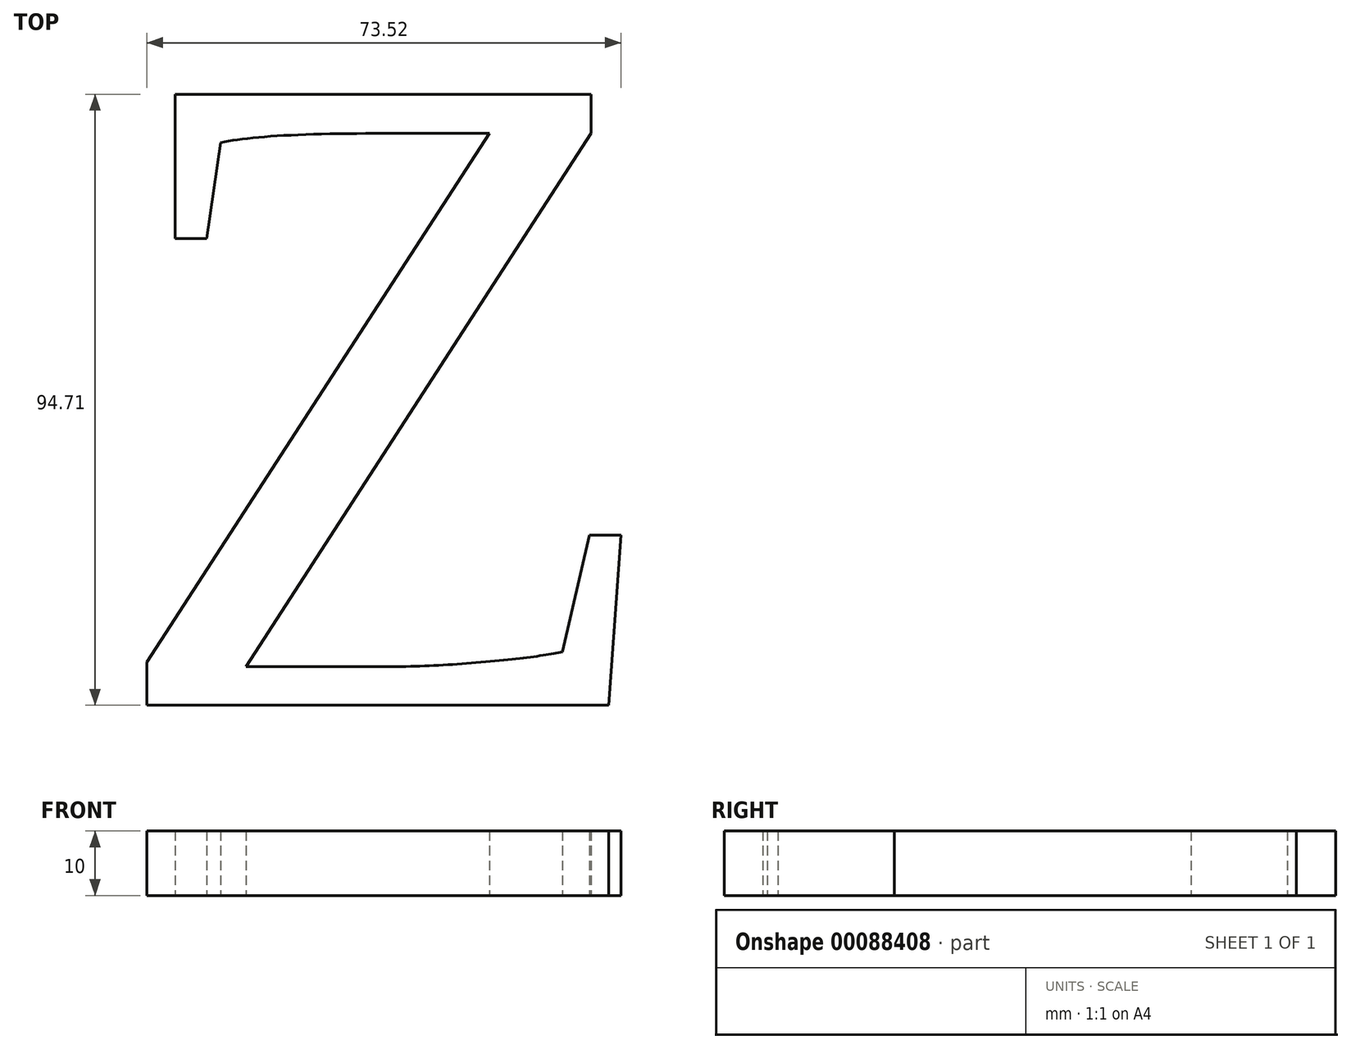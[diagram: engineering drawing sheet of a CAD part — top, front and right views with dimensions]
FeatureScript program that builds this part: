
annotation { "Feature Type Name" : "Feature", "Feature Type Description" : "" }
export const myFeature = defineFeature(function(context is Context, id is Id, definition is map)
    precondition{}
    {
        {
            var Q0;
            Q0=qCreatedBy(makeId("Top.planeOp"),FACE);
            var sketch = newSketch(context, id + "F0", { "sketchPlane" : qUnion([Q0])});
            skText(sketch, "E0", { "text": "Z", "fontName": "Tinos-Regular.ttf"});
            const initialGuessF0  = {"E0": [-0.0708, -0.04558, 1, 0, 0.10413]};
            skSetInitialGuess(sketch, initialGuessF0);
            skSolve(sketch);
        }
        {
            var Q0;
            Q0 = qSketchRegion(id + "F0", true);
            extrude(context, id + "F1", {"entities" : qUnion([Q0]), "depth" : 10 * mm});
        }
    });
